# Revit family: CIVIC WALL MOUNT 90MM PUSH TIME FLOW
name_source: partatom
category: Plumbing Fixtures
units: mm (PartAtom-declared; Revit-internal decimal feet)

## family parameters
Cut with Voids When Loaded = Yes
Host = Face
OmniClass Number = 23.45.55.14
OmniClass Title = Single Faucets
Part Type = Normal
Room Calculation Point = No
Round Connector Dimension = Use Diameter
Shared = No

## types (3) — shared parameters
Assembly Code = D2020300
Base_Material = GWA_Metal-Chrome
CW Connection = Yes
HW Connection = Yes
Manufacturer = GWA Bathrooms & Kitchens
Model = 96414C6A
URL = https://www.caroma.com.au
Vent Connection = No
Waste Connection = No
zero-valued in all types: Default Elevation

## per-type parameters (varying)
| type | Indicator_Colour |
| CIVIC WALL MOUNT 90MM PUSH TIME FLOW - HOT | GWA-Plastic-Red |
| CIVIC WALL MOUNT 90MM PUSH TIME FLOW - COLD | GWA-Plastic-Blue |
| CIVIC WALL MOUNT 90MM PUSH TIME FLOW - WARM | GWA-Plastic-Yellow |

note: column(s) folded — value = type name in every type: Description

## geometry (parser evidence)
native form markers: Sweep x2
no freeform markers — native parametric forms only
